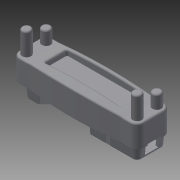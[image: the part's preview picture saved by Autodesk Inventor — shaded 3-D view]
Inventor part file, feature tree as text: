
AUTODESK INVENTOR PART (.ipt)
format: ipt  version: 2014 (Build 180170000, 170)  size: 678,912 bytes
history: native  units: mm
features: sketch x18, extrude x17, fillet x3, sweep x1, shell x1
ambient origin geometry x8: Origin, YZ Plane, XZ Plane, XY Plane, X Axis, Y Axis, Z Axis, Center Point
bodies: Solid1 (feature_tree)
feature tree (40):
  extrude  "Extrusion1"  Depth=38.0mm
  extrude  "Extrusion2"  Depth=70.0mm
  extrude  "Extrusion4"  Depth=8.0mm
  extrude  "Extrusion5"  Depth=5.0mm
  extrude  "Extrusion6"  Depth=5.0mm
  sweep  "Sweep1"
  extrude  "Extrusion7"  Depth=15.0mm
  extrude  "Extrusion8"  Depth=2.0mm
  extrude  "Extrusion12"  Depth=2.0mm
  shell  "Shell1"  Thickness=2.0mm
  extrude  "Extrusion9"  Depth=10.0mm
  extrude  "Extrusion10"  Depth=13.5mm
  extrude  "Extrusion11"  Depth=3.0mm
  fillet  "Fillet3"  Radius=9.0mm
  fillet  "Fillet4"  Radius=3.0mm
  extrude  "Extrusion13"  TaperAngle=0.0deg  [1 undecoded]
  extrude  "Extrusion14"  TaperAngle=45.0deg  [1 undecoded]
  extrude  "Extrusion15"  Depth=25.0mm
  extrude  "Extrusion16"  TaperAngle=0.0deg  [1 undecoded]
  extrude  "Extrusion17"  TaperAngle=0.0deg  [1 undecoded]
  extrude  "Extrusion18"  Depth=20.0mm
  fillet  "Fillet5"  [1 undecoded]
  sketch  "Sketch2"  dims[d0=19.0mm d1=38.0mm]
  sketch  "Sketch4"  dims[d2=140.0mm d3=70.0mm]
  sketch  "Sketch5"  dims[d4=8.0mm d5=8.0mm]
  sketch  "Sketch6"  dims[d6=5.0mm d7=0.0mm d12=3.5mm]
  sketch  "Sketch7"  dims[d17=5.0mm d18=0.0mm d24=30.0mm]
  sketch  "Sketch8"  dims[d25=30.0mm d26=18.0mm]
  sketch  "Sketch9"  dims[d27=15.0mm d28=15.0mm]
  sketch  "Sketch10"  dims[d30=2.0mm d31=18.0mm]
  sketch  "Sketch11"  dims[d32=5.5mm d33=2.0mm d34=2.0mm]
  sketch  "Sketch12"  dims[d35=2.0mm d36=10.0mm]
  sketch  "Sketch13"  dims[d37=6.0mm d38=13.5mm d39=-0.872665mm]
  sketch  "Sketch14"  dims[d41=54.0mm d42=16.0mm d43=9.0mm d44=3.0mm]
  sketch  "Sketch15"  dims[d45=15.0mm d46=0.0mm d47=0.0mm]
  sketch  "Sketch16"  dims[d48=0.0mm d50=45.0deg]
  sketch  "Sketch17"  dims[d51=15.0mm d52=25.0mm]
  sketch  "Sketch18"  dims[d53=12.5mm d54=0.0mm d55=0.0mm]
  sketch  "Sketch19"  dims[d56=45.0deg d57=0.0mm]
  sketch  "Sketch20"  dims[d58=0.0mm d59=20.0mm d60=0.0mm d61=15.0mm d63=33.0mm d64=6.1mm d65=6.1mm d66=10.0mm d67=10.0mm d68=2.0mm d69=2.0mm d70=1.0mm d71=1.0mm d74=60.0mm d75=4.0mm d76=0.0mm d77=6.0mm d78=6.0mm d79=2.0mm d80=2.0mm d81=1.0mm d82=1.0mm d83=0.0mm d85=33.0mm d86=10.0mm d87=10.0mm d88=64.0mm d89=4.0mm d90=0.0mm d91=1.5mm d92=15.0mm d93=7.5mm d94=12.0mm d95=10.0mm d96=0.0mm d97=15.0mm d98=3.0mm d99=14.0mm d100=0.0mm d101=10.0mm d102=0.0mm d103=3.0mm d105=5.0mm d107=5.0mm d108=5.0mm d109=2.0mm d110=0.5mm d111=2.0mm d112=2.0mm d113=12.0mm d114=6.0mm d115=2.0mm d116=0.0mm d117=2.5mm d118=7.0mm d119=10.0mm d120=13.0mm d121=50.0mm d122=0.0mm d123=20.0mm d124=0.0mm d125=10.0mm d126=10.0mm d127=15.0mm d128=0.0mm d129=10.0mm d130=10.0mm d131=25.0mm d132=0.0mm d133=85.0mm d134=25.0mm d135=42.5mm d136=4.0mm d137=5.0mm d138=0.0mm d139=15.0mm d140=15.0mm d142=38.0mm d143=3.0mm d144=0.0mm d145=110.0mm d146=34.144474mm d147=3.0mm d148=0.0mm d149=2.0mm]
note: 5 required parameter values undecoded (feature->parameter linkage not recoverable at this tier; creation-order binding heuristic only, values carry confidence <= 0.55)
